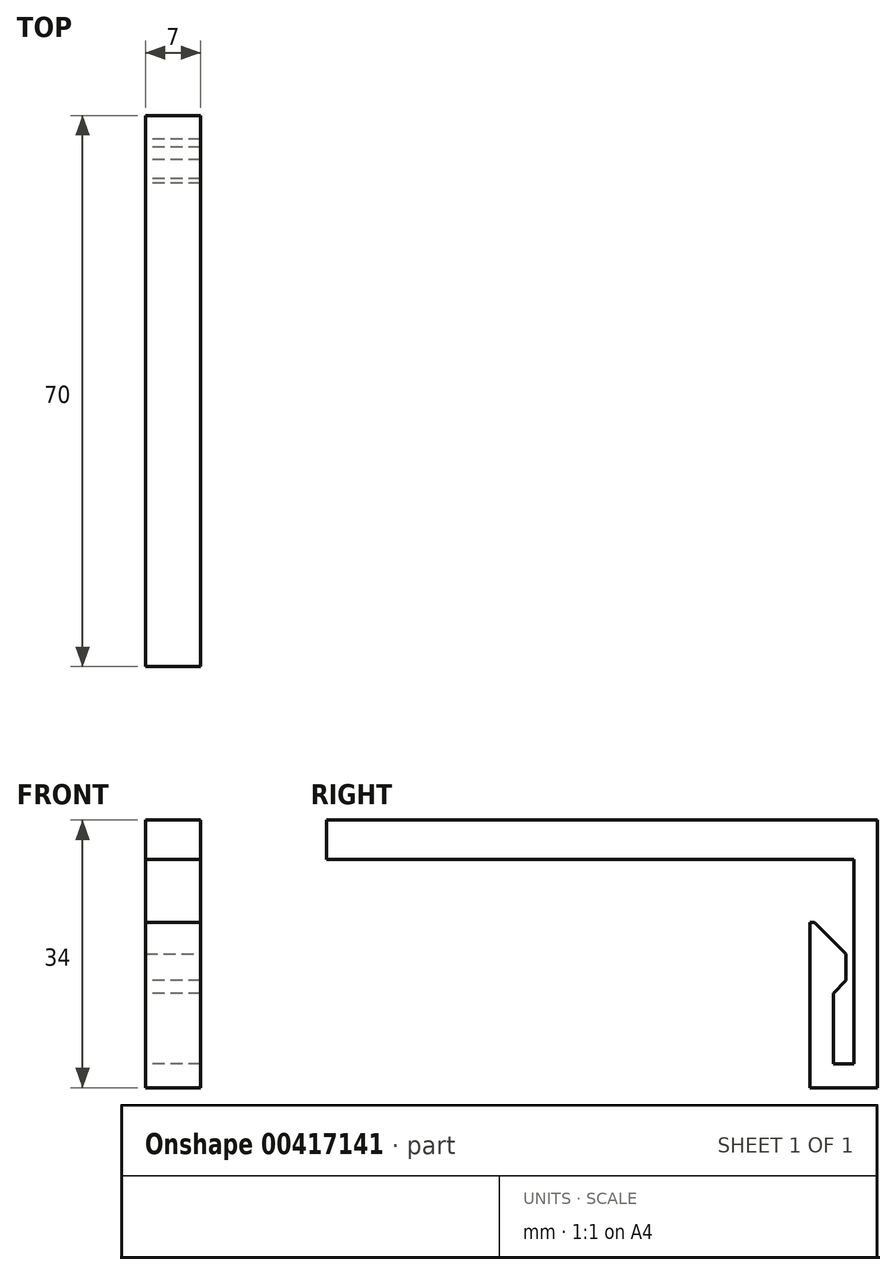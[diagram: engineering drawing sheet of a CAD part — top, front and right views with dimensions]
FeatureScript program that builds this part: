
annotation { "Feature Type Name" : "Feature", "Feature Type Description" : "" }
export const myFeature = defineFeature(function(context is Context, id is Id, definition is map)
    precondition{}
    {
        {
            var Q0;
            Q0=qCreatedBy(makeId("Top.planeOp"),FACE);
            var sketch = newSketch(context, id + "F0", { "sketchPlane" : qUnion([Q0])});
            skLineSegment(sketch, "E0.bottom", {"start": v(-3.5, 35) * mm, "end": v(3.5, 35) * mm});
            skLineSegment(sketch, "E0.top", {"start": v(-3.5, -35) * mm, "end": v(3.5, -35) * mm});
            skLineSegment(sketch, "E0.left", {"start": v(-3.5, 35) * mm, "end": v(-3.5, -35) * mm});
            skLineSegment(sketch, "E0.right", {"start": v(3.5, 35) * mm, "end": v(3.5, -35) * mm});
            skPoint(sketch, "E0.middle", {"position": v(0, 0) * mm});
            skSolve(sketch);
        }
        {
            var Q0;
            Q0 = qSketchRegion(id + "F0", true);
            extrude(context, id + "F1", {"entities" : qUnion([Q0]), "depth" : 5 * mm});
        }
        {
            var Q0;
            Q0=makeQuery(id+"F1.opExtrude","CAP_FACE",FACE,{"disambiguationData":[OSD([sQuery(id+"F0.wireOp",EDGE,"E0.bottom"),sQuery(id+"F0.wireOp",EDGE,"E0.top"),sQuery(id+"F0.wireOp",EDGE,"E0.left"),sQuery(id+"F0.wireOp",EDGE,"E0.right")])],"isStart":true});
            var sketch = newSketch(context, id + "F2", { "sketchPlane" : qUnion([Q0])});
            skLineSegment(sketch, "E1.bottom", {"start": v(3.5, -35) * mm, "end": v(-3.5, -35) * mm});
            skLineSegment(sketch, "E1.top", {"start": v(3.5, -32) * mm, "end": v(-3.5, -32) * mm});
            skLineSegment(sketch, "E1.left", {"start": v(3.5, -35) * mm, "end": v(3.5, -32) * mm});
            skLineSegment(sketch, "E1.right", {"start": v(-3.5, -35) * mm, "end": v(-3.5, -30) * mm});
            skSolve(sketch);
        }
        {
            var Q0;
            Q0 = qSketchRegion(id + "F2", true);
            extrude(context, id + "F3", {"entities" : qUnion([Q0]), "operationType" : NewBodyOperationType.ADD, "depth" : 26 * mm});
        }
        {
            var Q0;
            Q0=makeQuery(id+"F3.opExtrude","CAP_FACE",FACE,{"disambiguationData":[OSD([sQuery(id+"F2.wireOp",EDGE,"E1.bottom"),sQuery(id+"F2.wireOp",EDGE,"E1.top"),sQuery(id+"F2.wireOp",EDGE,"E1.left"),sQuery(id+"F2.wireOp",EDGE,"E1.right")])],"isStart":false});
            var sketch = newSketch(context, id + "F4", { "sketchPlane" : qUnion([Q0])});
            skLineSegment(sketch, "E2.bottom", {"start": v(3.5, -35) * mm, "end": v(-3.5, -35) * mm});
            skLineSegment(sketch, "E2.top", {"start": v(3.5, -26.4) * mm, "end": v(-3.5, -26.4) * mm});
            skLineSegment(sketch, "E2.left", {"start": v(3.5, -35) * mm, "end": v(3.5, -26.4) * mm});
            skLineSegment(sketch, "E2.right", {"start": v(-3.5, -35) * mm, "end": v(-3.5, -26.4) * mm});
            skSolve(sketch);
        }
        {
            var Q0;
            Q0 = qSketchRegion(id + "F4", true);
            extrude(context, id + "F5", {"entities" : qUnion([Q0]), "operationType" : NewBodyOperationType.ADD, "depth" : 3 * mm});
        }
        {
            var Q0;
            Q0=makeQuery(id+"F5.opExtrude","CAP_FACE",FACE,{"disambiguationData":[OSD([sQuery(id+"F4.wireOp",EDGE,"E2.bottom"),sQuery(id+"F4.wireOp",EDGE,"E2.top"),sQuery(id+"F4.wireOp",EDGE,"E2.left"),sQuery(id+"F4.wireOp",EDGE,"E2.right")])],"isStart":true});
            var sketch = newSketch(context, id + "F6", { "sketchPlane" : qUnion([Q0])});
            skLineSegment(sketch, "E3.bottom", {"start": v(3.5, 26.4) * mm, "end": v(-3.5, 26.4) * mm});
            skLineSegment(sketch, "E3.top", {"start": v(3.5, 29.4) * mm, "end": v(-3.5, 29.4) * mm});
            skLineSegment(sketch, "E3.left", {"start": v(3.5, 26.4) * mm, "end": v(3.5, 29.4) * mm});
            skLineSegment(sketch, "E3.right", {"start": v(-3.5, 26.4) * mm, "end": v(-3.5, 29.4) * mm});
            skSolve(sketch);
        }
        {
            var Q0;
            Q0 = qSketchRegion(id + "F6", true);
            extrude(context, id + "F7", {"entities" : qUnion([Q0]), "operationType" : NewBodyOperationType.ADD, "depth" : 18 * mm});
        }
        {
            var Q0;
            Q0=makeQuery(id+"F7.opExtrude","SWEPT_FACE",FACE,{"disambiguationData":[OSD([sQuery(id+"F6.wireOp",EDGE,"E3.top")])]});
            var sketch = newSketch(context, id + "F8", { "sketchPlane" : qUnion([Q0])});
            skLineSegment(sketch, "E4.bottom", {"start": v(-3.5, -8) * mm, "end": v(3.5, -8) * mm});
            skLineSegment(sketch, "E4.top", {"start": v(-3.5, -17) * mm, "end": v(3.5, -17) * mm});
            skLineSegment(sketch, "E4.left", {"start": v(-3.5, -8) * mm, "end": v(-3.5, -17) * mm});
            skLineSegment(sketch, "E4.right", {"start": v(3.5, -8) * mm, "end": v(3.5, -17) * mm});
            skSolve(sketch);
        }
        {
            var Q0;
            Q0 = qSketchRegion(id + "F8", true);
            extrude(context, id + "F9", {"entities" : qUnion([Q0]), "operationType" : NewBodyOperationType.ADD, "depth" : 1.6 * mm});
        }
        {
            var Q0;
            Q0=makeQuery(id+"F9.opExtrude","CAP_EDGE",EDGE,{"disambiguationData":[OSD([sQuery(id+"F8.wireOp",EDGE,"E4.bottom")])],"isStart":false});
            chamfer(context, id + "F10", {"entities" : qUnion([Q0]), "width" : 4 * mm, "tangentPropagation" : true});
        }
        {
            var Q0;
            Q0=makeQuery(id+"F9.opExtrude","CAP_EDGE",EDGE,{"disambiguationData":[OSD([sQuery(id+"F8.wireOp",EDGE,"E4.top")])],"isStart":false});
            chamfer(context, id + "F11", {"entities" : qUnion([Q0]), "width" : 1.6 * mm, "tangentPropagation" : true});
        }
    });
